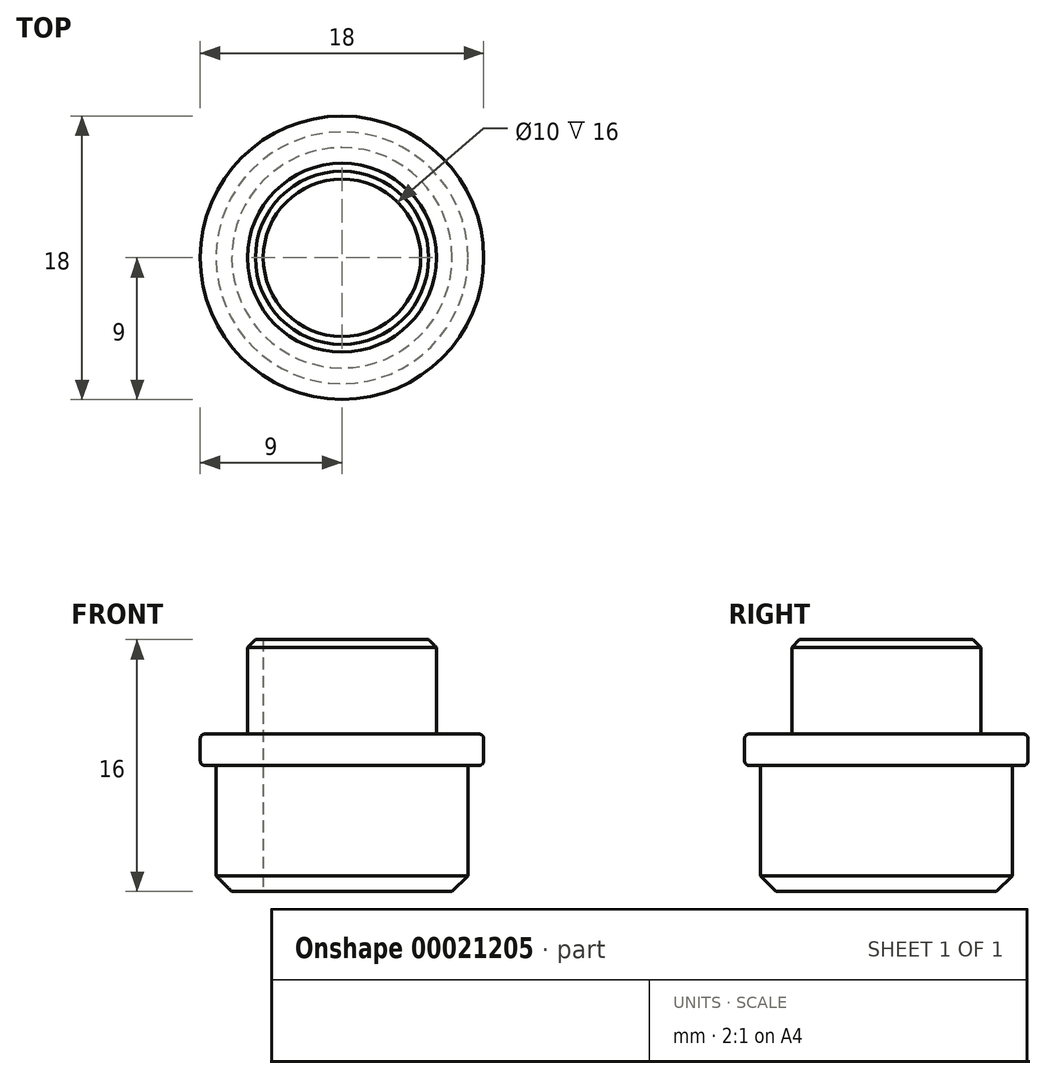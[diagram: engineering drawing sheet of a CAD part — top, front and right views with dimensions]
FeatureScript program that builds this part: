
annotation { "Feature Type Name" : "Feature", "Feature Type Description" : "" }
export const myFeature = defineFeature(function(context is Context, id is Id, definition is map)
    precondition{}
    {
        {
            var Q0;
            Q0=qCreatedBy(makeId("Top.planeOp"),FACE);
            var sketch = newSketch(context, id + "F0", { "sketchPlane" : qUnion([Q0])});
            skCircle(sketch, "E0", {"center": v(0, 0) * mm, "radius": 9 * mm});
            skSolve(sketch);
        }
        {
            var Q0;
            Q0=qSketchRegion(id+"F0",true);
            extrude(context, id + "F1", {"entities" : qUnion([Q0]), "depth" : 2 * mm});
        }
        {
            var Q0;
            Q0=makeQuery(id+"F1.opExtrude","CAP_FACE",FACE,{"disambiguationData":[OSD([sQuery(id+"F0.wireOp",EDGE,"E0")])],"isStart":false});
            var sketch = newSketch(context, id + "F2", { "sketchPlane" : qUnion([Q0])});
            skCircle(sketch, "E1", {"center": v(0, 0) * mm, "radius": 6 * mm});
            skSolve(sketch);
        }
        {
            var Q0;
            Q0=qSketchRegion(id+"F2",true);
            extrude(context, id + "F3", {"entities" : qUnion([Q0]), "operationType" : NewBodyOperationType.ADD, "depth" : 6 * mm});
        }
        {
            var Q0;
            Q0=makeQuery(id+"F1.opExtrude","CAP_FACE",FACE,{"disambiguationData":[OSD([sQuery(id+"F0.wireOp",EDGE,"E0")])],"isStart":true});
            var sketch = newSketch(context, id + "F4", { "sketchPlane" : qUnion([Q0])});
            skCircle(sketch, "E2", {"center": v(0, 0) * mm, "radius": 8 * mm});
            skSolve(sketch);
        }
        {
            var Q0;
            Q0=qSketchRegion(id+"F4",true);
            extrude(context, id + "F5", {"entities" : qUnion([Q0]), "operationType" : NewBodyOperationType.ADD, "depth" : 8 * mm});
        }
        {
            var Q0;
            Q0=makeQuery(id+"F5.opExtrude","CAP_FACE",FACE,{"disambiguationData":[OSD([sQuery(id+"F4.wireOp",EDGE,"E2")])],"isStart":false});
            var sketch = newSketch(context, id + "F6", { "sketchPlane" : qUnion([Q0])});
            skCircle(sketch, "E3", {"center": v(0, 0) * mm, "radius": 5 * mm});
            skSolve(sketch);
        }
        {
            var Q0;
            Q0=qSketchRegion(id+"F6",true);
            extrude(context, id + "F7", {"entities" : qUnion([Q0]), "operationType" : NewBodyOperationType.REMOVE, "endBound" : BoundingType.THROUGH_ALL, "oppositeDirection" : true, "depth" : 25 * mm});
        }
        {
            var Q0;
            Q0=makeQuery(id+"F5.opExtrude","CAP_EDGE",EDGE,{"disambiguationData":[OSD([sQuery(id+"F4.wireOp",EDGE,"E2")])],"isStart":false});
            chamfer(context, id + "F8", {"entities" : qUnion([Q0]), "width" : 1 * mm, "tangentPropagation" : true});
        }
        {
            var Q0;
            Q0=makeQuery(id+"F3.opExtrude","CAP_EDGE",EDGE,{"disambiguationData":[OSD([sQuery(id+"F2.wireOp",EDGE,"E1")])],"isStart":false});
            chamfer(context, id + "F9", {"entities" : qUnion([Q0]), "width" : 0.5 * mm, "tangentPropagation" : true});
        }
        {
            var Q0;
            Q0=makeQuery(id+"F1.opExtrude","CAP_EDGE",EDGE,{"disambiguationData":[OSD([sQuery(id+"F0.wireOp",EDGE,"E0")])],"isStart":true});
            var Q1;
            Q1=makeQuery(id+"F1.opExtrude","CAP_EDGE",EDGE,{"disambiguationData":[OSD([sQuery(id+"F0.wireOp",EDGE,"E0")])],"isStart":false});
            fillet(context, id + "F10", {"entities" : qUnion([Q0, Q1]), "radius" : 0.3 * mm, "tangentPropagation" : true, "allowEdgeOverflow" : false});
        }
    });
